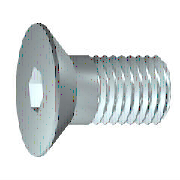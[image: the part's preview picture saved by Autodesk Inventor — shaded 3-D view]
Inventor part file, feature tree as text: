
AUTODESK INVENTOR PART (.ipt)
format: ipt  version: 2019 (Build 230136000, 136)  size: 180,736 bytes
history: native  units: mm (DEFAULTED — no unit token found)
features: sketch x2, extrude x1, plane x1
ambient origin geometry x7: Origin, YZ Plane, XY Plane, X Axis, Y Axis, Z Axis, Center Point
bodies: Solid1 (feature_tree), Body (feature_tree)
feature tree (4):
  sketch  "Sketch2"  dims[d2=2.67mm d3=6.0mm d6=3.72mm d7=45.0deg d8=4.618802mm d9=60.0deg d10=11.34mm d11=6.0mm d12=0.61345mm d13=90.0deg d30=10.0mm d14=0.0mm d15=18.0mm d16=0.0mm d17=0.61345mm d18=0.61345mm d20=0.0mm d39=45.0deg d43=0.0mm d44=0.0mm]
  extrude  "Slot"  Depth=18.0mm
  plane  "Work Plane1"
  sketch  "Sketch1"  dims[d0=25.0mm d1=18.0mm]
